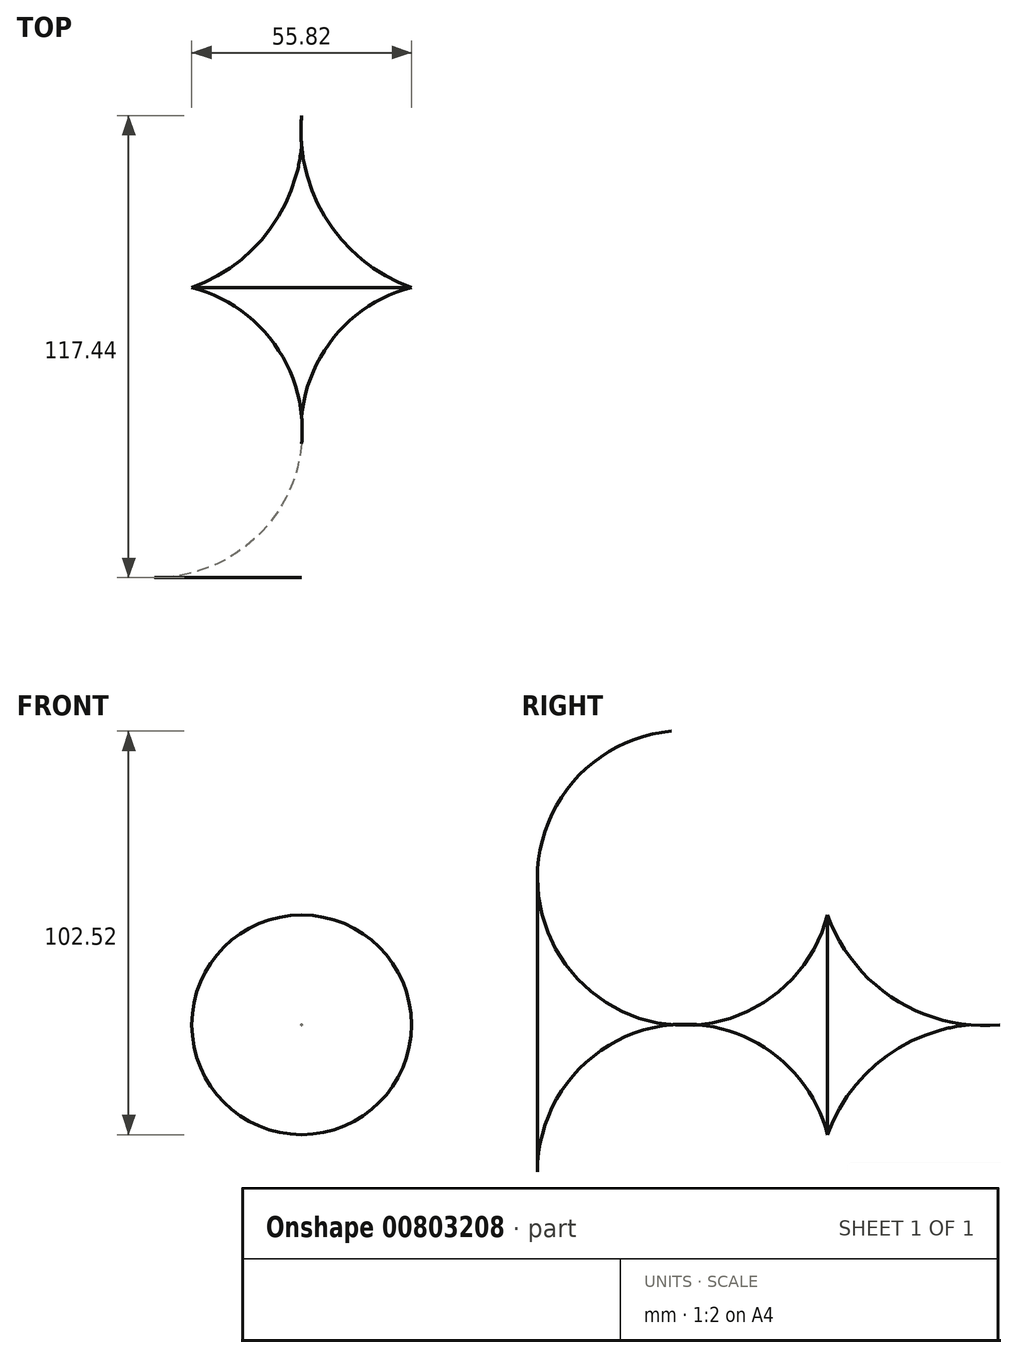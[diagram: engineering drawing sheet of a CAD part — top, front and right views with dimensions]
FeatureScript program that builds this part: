
annotation { "Feature Type Name" : "Feature", "Feature Type Description" : "" }
export const myFeature = defineFeature(function(context is Context, id is Id, definition is map)
    precondition{}
    {
        {
            var Q0;
            Q0=qCreatedBy(makeId("Top.planeOp"),FACE);
            var sketch = newSketch(context, id + "F0", { "sketchPlane" : qUnion([Q0])});
            skLineSegment(sketch, "E0", {"start": v(0, 55.07) * mm, "end": v(0, -59.34) * mm, "construction": true});
            skArc(sketch, "E1", {"start": v(27.9, 0) * mm, "mid": v(8.76, -12) * mm, "end": v(0, -32.82) * mm});
            skArc(sketch, "E2", {"start": v(0, 35.97) * mm, "mid": v(8.7, 13.91) * mm, "end": v(27.9, 0) * mm});
            skLineSegment(sketch, "E3", {"start": v(0, 35.97) * mm, "end": v(0, -32.82) * mm});
            skSolve(sketch);
        }
        {
            var Q0;
            Q0=makeQuery(id+"F0.imprint","IMPRINT",FACE,{"disambiguationData":[TD([[makeQuery(id+"F0.imprint","IMPRINT",EDGE,{"derivedFrom":sQuery(id+"F0.wireOp",EDGE,"E1")}),-1.0]])]});
            var Q1;
            Q1=sQuery(id+"F0.wireOp",EDGE,"E0");
            revolve(context, id + "F1", {"surfaceOperationType" : NewSurfaceOperationType.NEW, "entities" : qUnion([Q0]), "axis" : qUnion([Q1]), "revolveType" : RevolveType.FULL});
        }
    });
